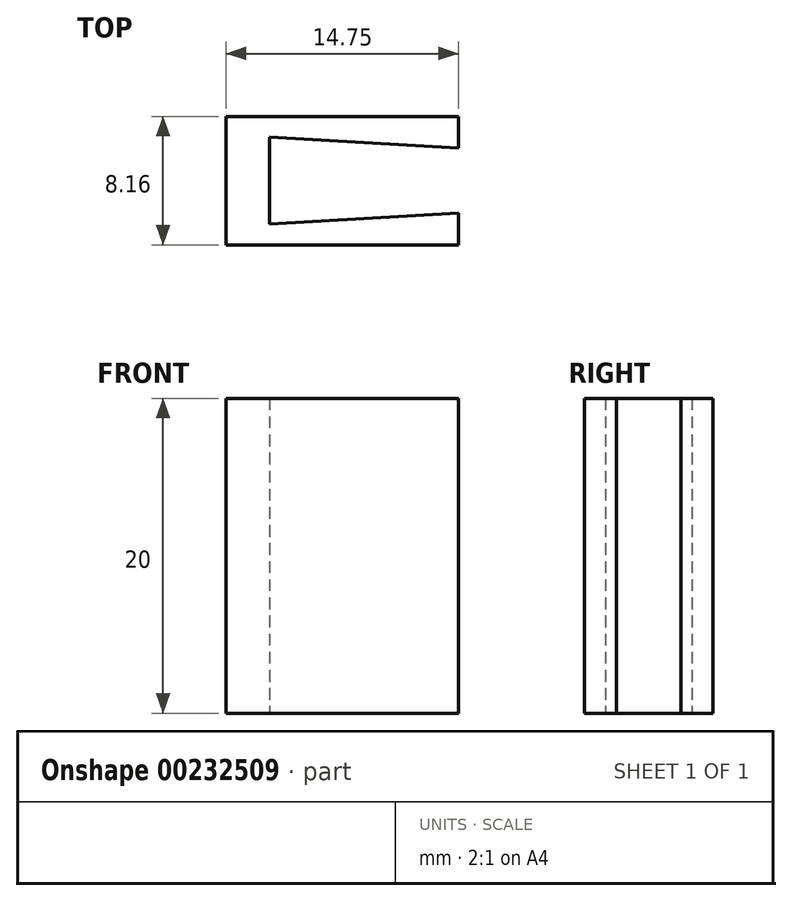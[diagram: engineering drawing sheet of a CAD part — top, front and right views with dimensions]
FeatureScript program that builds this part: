
annotation { "Feature Type Name" : "Feature", "Feature Type Description" : "" }
export const myFeature = defineFeature(function(context is Context, id is Id, definition is map)
    precondition{}
    {
        {
            var Q0;
            Q0=qCreatedBy(makeId("Top.planeOp"),FACE);
            var sketch = newSketch(context, id + "F0", { "sketchPlane" : qUnion([Q0])});
            skLineSegment(sketch, "E0.bottom", {"start": v(-26.88, -2.73) * mm, "end": v(-29.63, -2.73) * mm});
            skLineSegment(sketch, "E0.top", {"start": v(-26.88, -8.23) * mm, "end": v(-29.63, -8.23) * mm});
            skLineSegment(sketch, "E0.left", {"start": v(-26.88, -2.73) * mm, "end": v(-26.88, -8.23) * mm});
            skLineSegment(sketch, "E0.right", {"start": v(-29.63, -2.73) * mm, "end": v(-29.63, -8.23) * mm});
            skLineSegment(sketch, "E1", {"start": v(-29.63, -2.73) * mm, "end": v(-29.63, -1.4) * mm});
            skLineSegment(sketch, "E2", {"start": v(-29.63, -1.4) * mm, "end": v(-26.88, -1.4) * mm});
            skLineSegment(sketch, "E3", {"start": v(-26.88, -1.4) * mm, "end": v(-26.88, -2.73) * mm});
            skLineSegment(sketch, "E4", {"start": v(-26.88, -1.4) * mm, "end": v(-14.88, -1.4) * mm});
            skLineSegment(sketch, "E5", {"start": v(-29.63, -8.23) * mm, "end": v(-29.63, -9.56) * mm});
            skLineSegment(sketch, "E6", {"start": v(-29.63, -9.56) * mm, "end": v(-26.88, -9.56) * mm});
            skLineSegment(sketch, "E7", {"start": v(-26.88, -9.56) * mm, "end": v(-26.88, -8.23) * mm});
            skLineSegment(sketch, "E8", {"start": v(-26.88, -9.56) * mm, "end": v(-14.88, -9.56) * mm});
            skLineSegment(sketch, "E9", {"start": v(-14.88, -1.4) * mm, "end": v(-14.88, -9.56) * mm});
            skLineSegment(sketch, "E10", {"start": v(-14.88, -1.4) * mm, "end": v(-14.88, -2.71) * mm});
            skLineSegment(sketch, "E11", {"start": v(-14.88, -2.71) * mm, "end": v(-14.88, -7.86) * mm});
            skLineSegment(sketch, "E12", {"start": v(-14.88, -7.86) * mm, "end": v(-14.88, -9.56) * mm});
            skLineSegment(sketch, "E13", {"start": v(-29.63, -1.4) * mm, "end": v(-29.63, -9.56) * mm});
            skLineSegment(sketch, "E14", {"start": v(-26.88, -2.73) * mm, "end": v(-14.88, -3.42) * mm});
            skLineSegment(sketch, "E15", {"start": v(-26.88, -8.23) * mm, "end": v(-14.88, -7.54) * mm});
            skSolve(sketch);
        }
        {
            var Q0;
            {var subQ0=sQuery(id+"F0.wireOp",EDGE,"E0.bottom");Q0=makeQuery(id+"F0.imprint","IMPRINT",FACE,{"disambiguationData":[TD([[makeQuery(id+"F0.imprint","IMPRINT",EDGE,{"derivedFrom":subQ0}),-1.0]])]});}
            var Q1;
            {var subQ0=sQuery(id+"F0.wireOp",EDGE,"E0.top");Q1=makeQuery(id+"F0.imprint","IMPRINT",FACE,{"disambiguationData":[TD([[makeQuery(id+"F0.imprint","IMPRINT",EDGE,{"derivedFrom":subQ0}),1.0]])]});}
            var Q2;
            Q2=makeQuery(id+"F0.imprint","IMPRINT",FACE,{"disambiguationData":[TD([[makeQuery(id+"F0.imprint","IMPRINT",EDGE,{"derivedFrom":sQuery(id+"F0.wireOp",EDGE,"E3")}),1.0]])]});
            var Q3;
            Q3=makeQuery(id+"F0.imprint","IMPRINT",FACE,{"disambiguationData":[TD([[makeQuery(id+"F0.imprint","IMPRINT",EDGE,{"derivedFrom":sQuery(id+"F0.wireOp",EDGE,"E7")}),-1.0]])]});
            var Q4;
            {var subQ0=sQuery(id+"F0.wireOp",EDGE,"E0.bottom");Q4=makeQuery(id+"F0.imprint","IMPRINT",FACE,{"disambiguationData":[TD([[makeQuery(id+"F0.imprint","IMPRINT",EDGE,{"derivedFrom":subQ0}),1.0]])]});}
            extrude(context, id + "F1", {"entities" : qUnion([Q0, Q1, Q2, Q3, Q4]), "depth" : 20 * mm});
        }
    });
